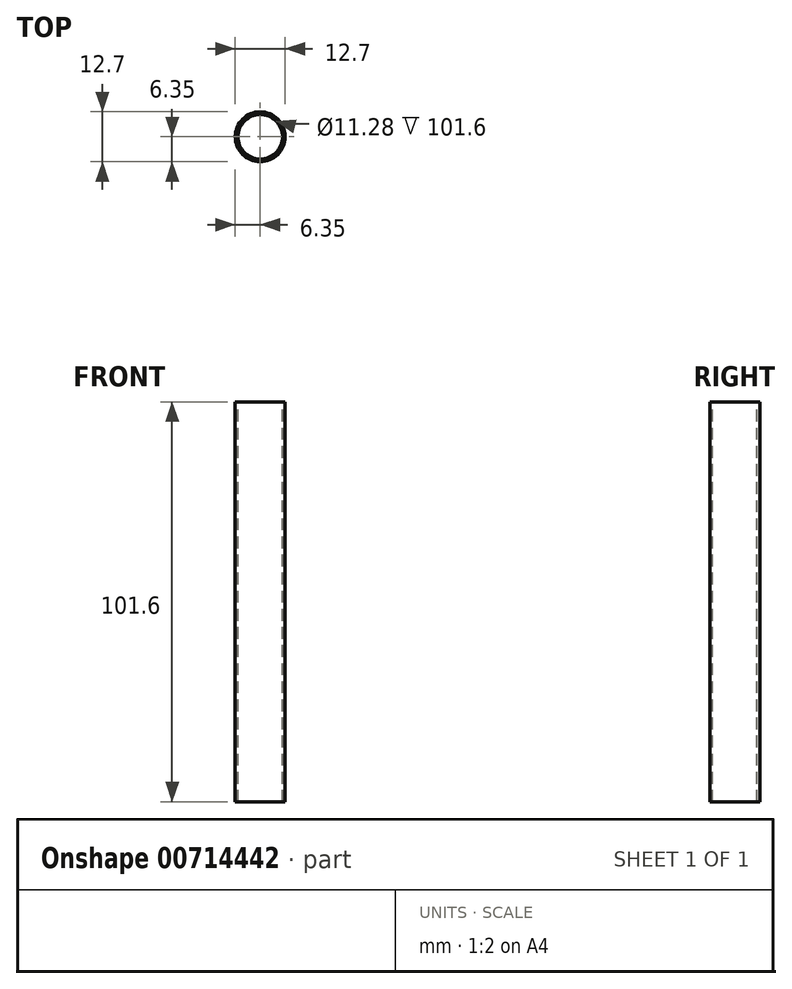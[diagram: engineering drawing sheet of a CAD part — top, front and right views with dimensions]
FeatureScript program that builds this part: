
annotation { "Feature Type Name" : "Feature", "Feature Type Description" : "" }
export const myFeature = defineFeature(function(context is Context, id is Id, definition is map)
    precondition{}
    {
        {
            var Q0;
            Q0=qCreatedBy(makeId("Top.planeOp"),FACE);
            var sketch = newSketch(context, id + "F0", { "sketchPlane" : qUnion([Q0])});
            skCircle(sketch, "E0", {"center": v(0, 0) * mm, "radius": 6.35 * mm});
            skCircle(sketch, "E1", {"center": v(0, 0) * mm, "radius": 5.64 * mm});
            skSolve(sketch);
        }
        {
            var Q0;
            Q0=qSketchRegion(id+"F0",true);
            extrude(context, id + "F1", {"entities" : qUnion([Q0]), "oppositeDirection" : true, "depth" : 101.6 * mm});
        }
    });
